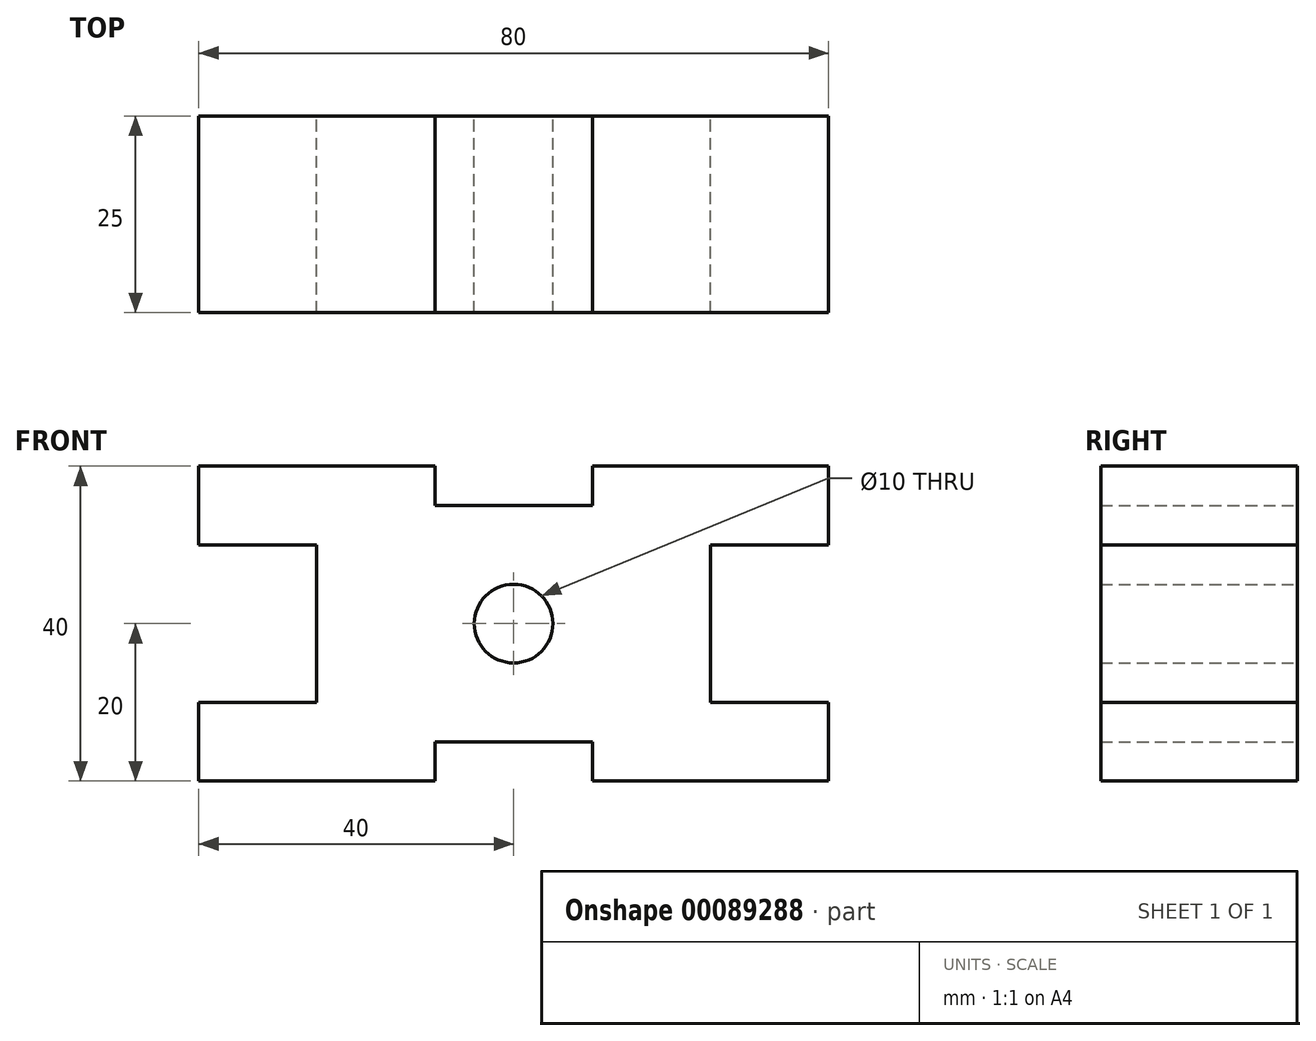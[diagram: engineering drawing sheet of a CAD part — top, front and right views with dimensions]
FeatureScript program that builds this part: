
annotation { "Feature Type Name" : "Feature", "Feature Type Description" : "" }
export const myFeature = defineFeature(function(context is Context, id is Id, definition is map)
    precondition{}
    {
        {
            var Q0;
            Q0=qCreatedBy(makeId("Front.planeOp"),FACE);
            var sketch = newSketch(context, id + "F0", { "sketchPlane" : qUnion([Q0])});
            skCircle(sketch, "E0", {"center": v(0, 0) * mm, "radius": 5 * mm});
            skLineSegment(sketch, "E1", {"start": v(0, 0) * mm, "end": v(0, 78.66) * mm, "construction": true});
            skLineSegment(sketch, "E2", {"start": v(0, 78.66) * mm, "end": v(0, -80.52) * mm, "construction": true});
            skLineSegment(sketch, "E3", {"start": v(0, 0) * mm, "end": v(-80.19, 0) * mm, "construction": true});
            skLineSegment(sketch, "E4", {"start": v(-80.19, 0) * mm, "end": v(80.32, 0) * mm, "construction": true});
            skLineSegment(sketch, "E5", {"start": v(10, -15) * mm, "end": v(10, -20) * mm});
            skLineSegment(sketch, "E6.MirrorCS", {"start": v(-10, -15) * mm, "end": v(-10, -20) * mm});
            skLineSegment(sketch, "E7.MirrorCS", {"start": v(10, 15) * mm, "end": v(10, 20) * mm});
            skLineSegment(sketch, "E8.MirrorCS", {"start": v(-10, 15) * mm, "end": v(-10, 20) * mm});
            skLineSegment(sketch, "E9", {"start": v(-10, -20) * mm, "end": v(-40, -20) * mm});
            skLineSegment(sketch, "E10.MirrorCS", {"start": v(10, -20) * mm, "end": v(40, -20) * mm});
            skLineSegment(sketch, "E11.MirrorCS", {"start": v(-10, 20) * mm, "end": v(-40, 20) * mm});
            skLineSegment(sketch, "E12.MirrorCS", {"start": v(10, 20) * mm, "end": v(40, 20) * mm});
            skLineSegment(sketch, "E13", {"start": v(-40, 20) * mm, "end": v(-40, 10) * mm});
            skLineSegment(sketch, "E14.MirrorCS", {"start": v(-40, -20) * mm, "end": v(-40, -10) * mm});
            skLineSegment(sketch, "E15", {"start": v(-40, -10) * mm, "end": v(-25, -10) * mm});
            skLineSegment(sketch, "E16.MirrorCS", {"start": v(-40, 10) * mm, "end": v(-25, 10) * mm});
            skLineSegment(sketch, "E17", {"start": v(-25, 10) * mm, "end": v(-25, -10) * mm});
            skLineSegment(sketch, "E18.MirrorCS", {"start": v(25, 10) * mm, "end": v(25, -10) * mm});
            skLineSegment(sketch, "E19.MirrorCS", {"start": v(40, 10) * mm, "end": v(25, 10) * mm});
            skLineSegment(sketch, "E20.MirrorCS", {"start": v(40, -10) * mm, "end": v(25, -10) * mm});
            skLineSegment(sketch, "E21.MirrorCS", {"start": v(40, -20) * mm, "end": v(40, -10) * mm});
            skLineSegment(sketch, "E22.MirrorCS", {"start": v(40, 20) * mm, "end": v(40, 10) * mm});
            skLineSegment(sketch, "E23", {"start": v(-10, 15) * mm, "end": v(10, 15) * mm});
            skLineSegment(sketch, "E24", {"start": v(-10, -15) * mm, "end": v(10, -15) * mm});
            skSolve(sketch);
        }
        {
            var Q0;
            Q0 = qSketchRegion(id + "F0", true);
            extrude(context, id + "F1", {"entities" : qUnion([Q0]), "depth" : 25 * mm});
        }
    });
